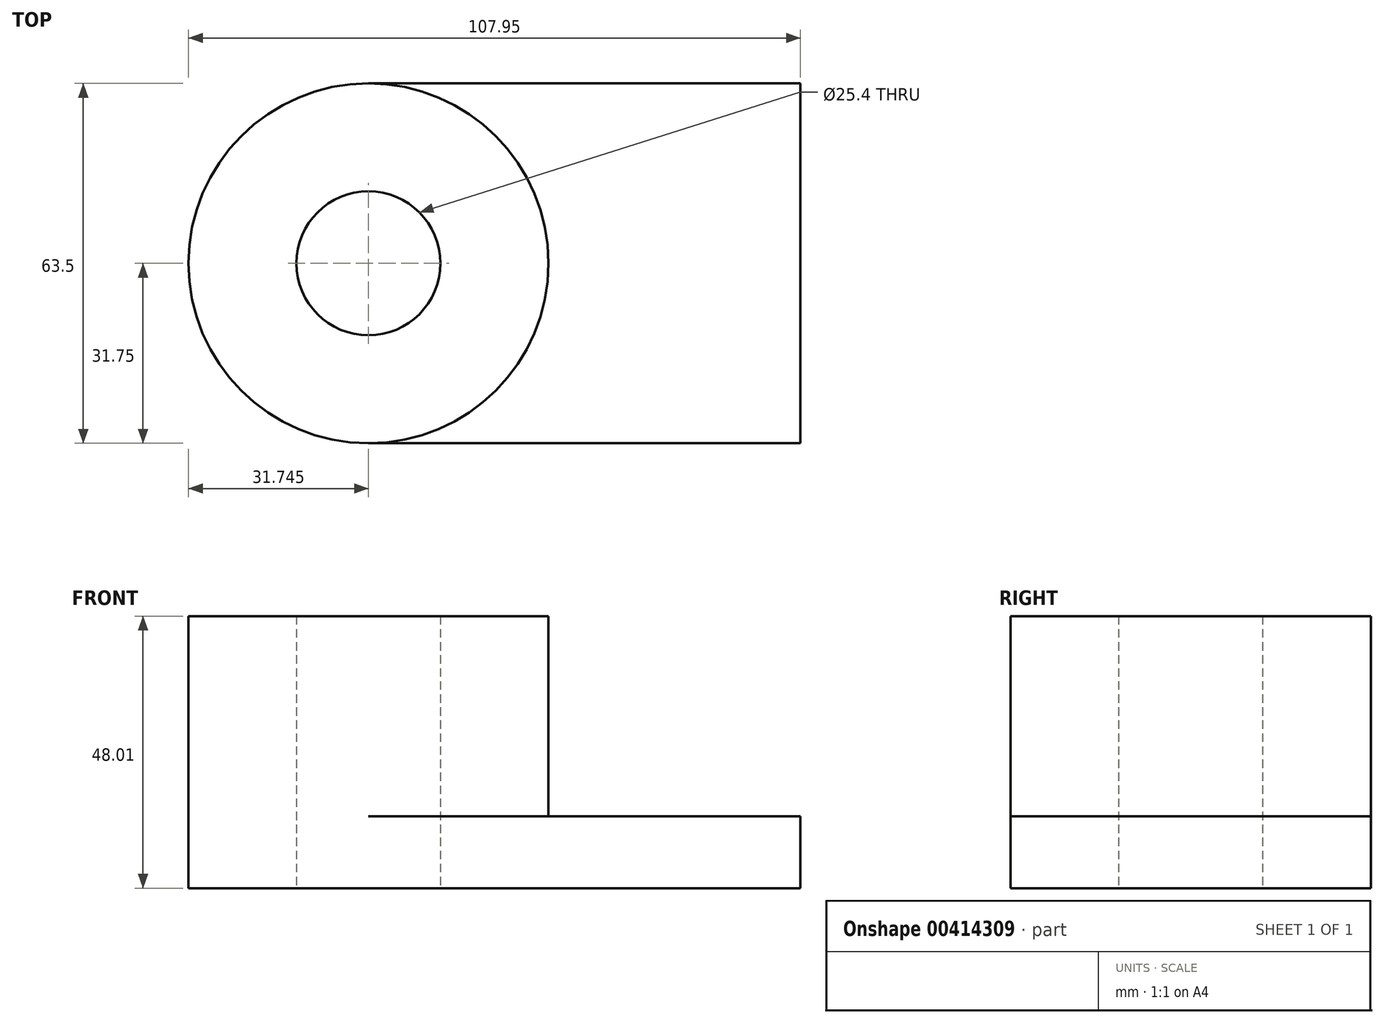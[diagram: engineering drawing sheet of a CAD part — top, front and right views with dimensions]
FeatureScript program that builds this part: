
annotation { "Feature Type Name" : "Feature", "Feature Type Description" : "" }
export const myFeature = defineFeature(function(context is Context, id is Id, definition is map)
    precondition{}
    {
        {
            var Q0;
            Q0=qCreatedBy(makeId("Top.planeOp"),FACE);
            var sketch = newSketch(context, id + "F0", { "sketchPlane" : qUnion([Q0])});
            skLineSegment(sketch, "E0.bottom", {"start": v(-61.28, 31.75) * mm, "end": v(14.92, 31.75) * mm});
            skLineSegment(sketch, "E0.top", {"start": v(-61.28, -31.75) * mm, "end": v(14.92, -31.75) * mm});
            skLineSegment(sketch, "E0.left", {"start": v(-61.28, 31.75) * mm, "end": v(-61.28, -31.75) * mm});
            skLineSegment(sketch, "E0.right", {"start": v(14.92, 31.75) * mm, "end": v(14.92, -31.75) * mm});
            skCircle(sketch, "E1", {"center": v(-61.28, 0) * mm, "radius": 31.75 * mm});
            skPoint(sketch, "E1.centerSnap0", {"position": v(-61.28, 0) * mm});
            skCircle(sketch, "E2", {"center": v(-61.28, 0) * mm, "radius": 12.7 * mm});
            skSolve(sketch);
        }
        {
            var Q0;
            {var subQ1=sQuery(id+"F0.wireOp",EDGE,"E0.left");var subQ3=sQuery(id+"F0.wireOp",EDGE,"E2");var subQ4=makeQuery(id+"F0.imprint","INTERSECT",VERTEX,{"disambiguationData":[OD(0.0)],"derivedFrom":[subQ1,subQ3]});Q0=makeQuery(id+"F0.imprint","IMPRINT",FACE,{"disambiguationData":[TD([[makeQuery(id+"F0.imprint","IMPRINT",EDGE,{"disambiguationData":[TD([[subQ4,-1.0]])],"derivedFrom":subQ3}),-1.0]])]});}
            var Q1;
            {var subQ1=sQuery(id+"F0.wireOp",EDGE,"E0.left");var subQ3=sQuery(id+"F0.wireOp",EDGE,"E2");var subQ4=makeQuery(id+"F0.imprint","INTERSECT",VERTEX,{"disambiguationData":[OD(0.0)],"derivedFrom":[subQ1,subQ3]});Q1=makeQuery(id+"F0.imprint","IMPRINT",FACE,{"disambiguationData":[TD([[makeQuery(id+"F0.imprint","IMPRINT",EDGE,{"disambiguationData":[TD([[subQ4,1.0]])],"derivedFrom":subQ3}),-1.0]])]});}
            extrude(context, id + "F1", {"entities" : qUnion([Q0, Q1]), "depth" : 48 * mm});
        }
        {
            var Q0;
            {var subQ0=sQuery(id+"F0.wireOp",EDGE,"E0.bottom");Q0=makeQuery(id+"F0.imprint","IMPRINT",FACE,{"disambiguationData":[TD([[makeQuery(id+"F0.imprint","IMPRINT",EDGE,{"derivedFrom":subQ0}),-1.0]])]});}
            extrude(context, id + "F2", {"entities" : qUnion([Q0]), "operationType" : NewBodyOperationType.ADD, "depth" : 12.7 * mm});
        }
    });
